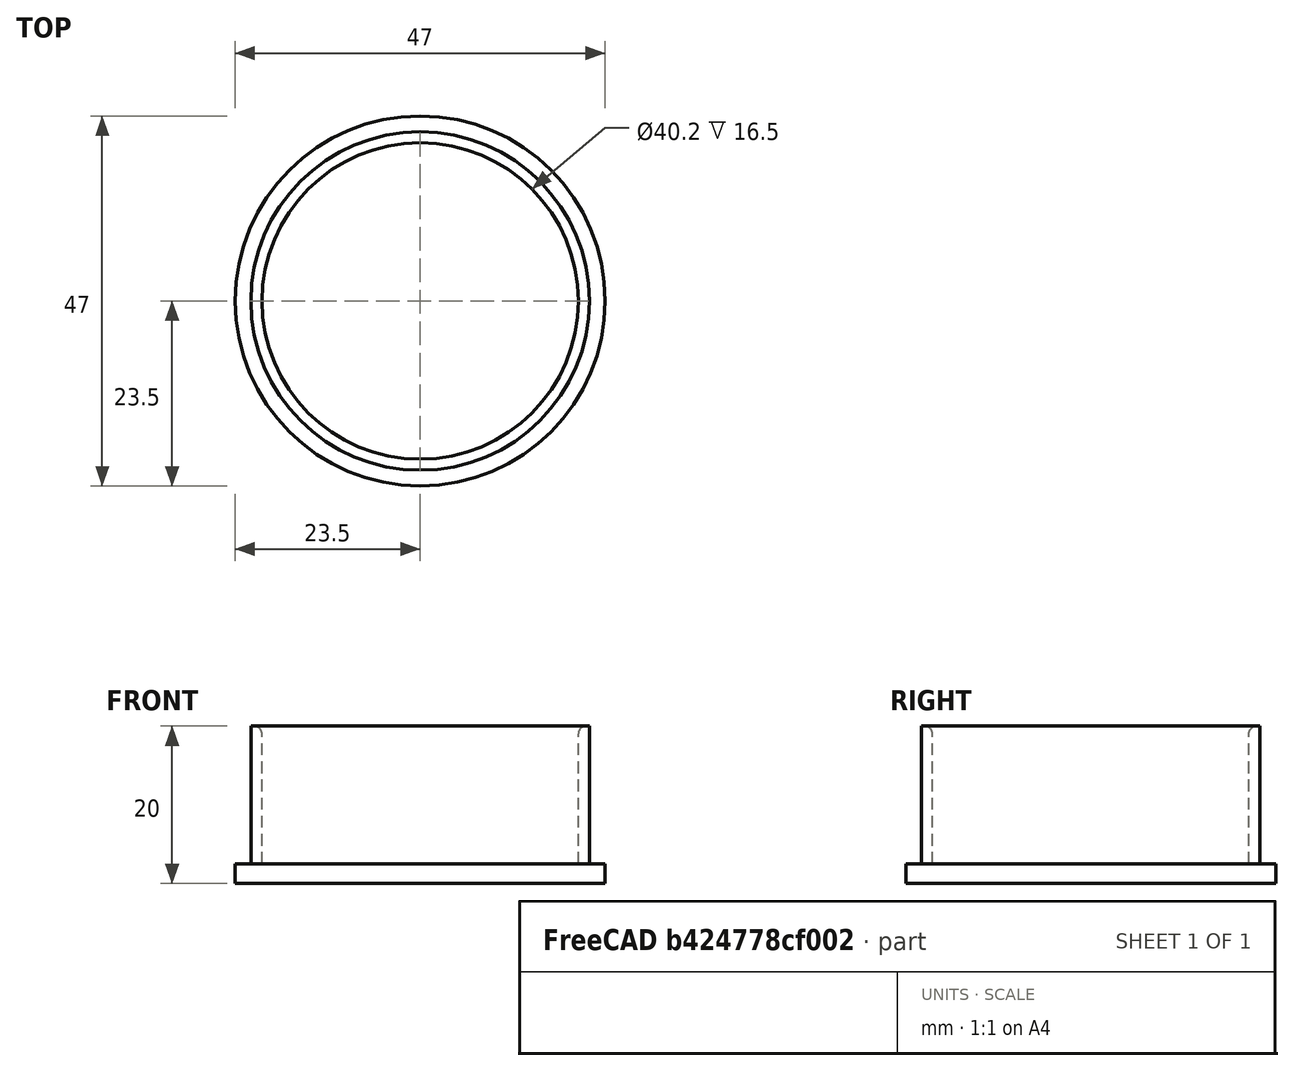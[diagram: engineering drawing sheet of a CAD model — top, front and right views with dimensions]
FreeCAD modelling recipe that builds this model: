
FCSTD DOCUMENT  (FreeCAD 0.17R13541 (Git))
Label: konvas-viewfinder-cap
License: All rights reserved
LicenseURL: http://en.wikipedia.org/wiki/All_rights_reserved
objects: Part::Cylinder×3, Part::Cut×1, Part::Fillet×1, Part::MultiFuse×1
note: 6 computed .brp shape members not serialized (recipe doc carries the construction recipe); baked Part::Feature solids carry a one-line shape summary decoded from their .brp

FEATURE [Part::Cylinder] Cylinder
  Angle = 360
  AttacherType = Attacher::AttachEngine3D
  Height = 2.5
  Radius = 23.5
FEATURE [Part::Cylinder] Cylinder001
  Angle = 360
  AttacherType = Attacher::AttachEngine3D
  Height = 20
  Radius = 21.5
FEATURE [Part::Cylinder] Cylinder002
  Angle = 360
  AttacherType = Attacher::AttachEngine3D
  Height = 30
  Placement = pos=(0,0,2.5) rot=(0,0,1;0rad)
  Radius = 20.1
FEATURE [Part::Cut] Cut
  Base = -> Cylinder001
  Tool = -> Cylinder002
FEATURE [Part::Fillet] Fillet
  Base = -> Cut
  Edges = 1 edges r=1: [Edge4]
FEATURE [Part::MultiFuse] Fusion
  Shapes = -> [Cylinder,Fillet]
